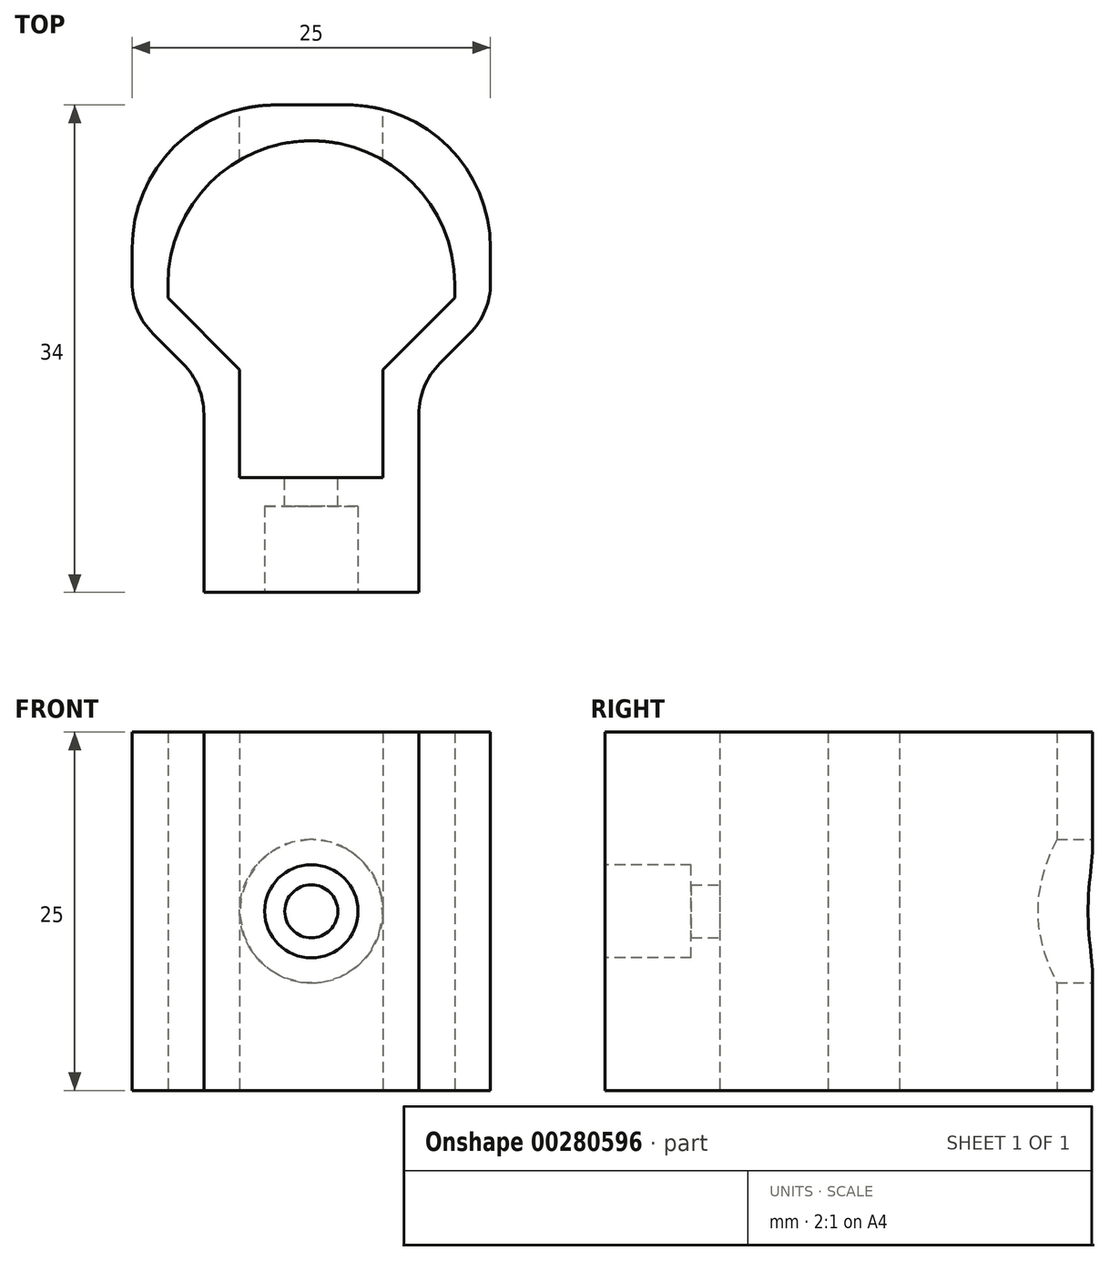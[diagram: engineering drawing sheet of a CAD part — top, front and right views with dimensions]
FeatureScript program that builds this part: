
annotation { "Feature Type Name" : "Feature", "Feature Type Description" : "" }
export const myFeature = defineFeature(function(context is Context, id is Id, definition is map)
    precondition{}
    {
        {
            var Q0;
            Q0=qCreatedBy(makeId("Top.planeOp"),FACE);
            var sketch = newSketch(context, id + "F0", { "sketchPlane" : qUnion([Q0])});
            skLineSegment(sketch, "E0", {"start": v(0, 0) * mm, "end": v(7.5, 0) * mm});
            skLineSegment(sketch, "E1", {"start": v(7.5, 0) * mm, "end": v(7.5, 14.5) * mm});
            skLineSegment(sketch, "E2", {"start": v(7.5, 14.5) * mm, "end": v(12.5, 14.5) * mm, "construction": true});
            skLineSegment(sketch, "E3", {"start": v(12.5, 14.5) * mm, "end": v(12.5, 19.5) * mm, "construction": true});
            skLineSegment(sketch, "E4", {"start": v(7.5, 14.5) * mm, "end": v(12.5, 19.5) * mm});
            skLineSegment(sketch, "E5", {"start": v(12.5, 34) * mm, "end": v(12.5, 19.5) * mm});
            skLineSegment(sketch, "E6", {"start": v(12.5, 34) * mm, "end": v(0, 34) * mm});
            skLineSegment(sketch, "E7.MirrorCS", {"start": v(-7.5, 14.5) * mm, "end": v(-12.5, 14.5) * mm, "construction": true});
            skLineSegment(sketch, "E8.MirrorCS", {"start": v(-12.5, 14.5) * mm, "end": v(-12.5, 19.5) * mm, "construction": true});
            skLineSegment(sketch, "E9.MirrorCS", {"start": v(-12.5, 34) * mm, "end": v(-12.5, 19.5) * mm});
            skLineSegment(sketch, "E10.MirrorCS", {"start": v(0, 0) * mm, "end": v(-7.5, 0) * mm});
            skLineSegment(sketch, "E11.MirrorCS", {"start": v(-7.5, 0) * mm, "end": v(-7.5, 14.5) * mm});
            skLineSegment(sketch, "E12.MirrorCS", {"start": v(-12.5, 34) * mm, "end": v(0, 34) * mm});
            skLineSegment(sketch, "E13.MirrorCS", {"start": v(-7.5, 14.5) * mm, "end": v(-12.5, 19.5) * mm});
            skLineSegment(sketch, "E14.0", {"start": v(-10, 21.5) * mm, "end": v(-10, 20.54) * mm});
            skLineSegment(sketch, "E14.1", {"start": v(-5, 15.54) * mm, "end": v(-10, 20.54) * mm});
            skLineSegment(sketch, "E14.2", {"start": v(0, 31.5) * mm, "end": v(0, 31.5) * mm});
            skLineSegment(sketch, "E14.3", {"start": v(-5, 8) * mm, "end": v(-5, 15.54) * mm});
            skLineSegment(sketch, "E14.6", {"start": v(0, 31.5) * mm, "end": v(0, 31.5) * mm});
            skLineSegment(sketch, "E14.7", {"start": v(10, 21.5) * mm, "end": v(10, 20.54) * mm});
            skLineSegment(sketch, "E14.8", {"start": v(5, 15.54) * mm, "end": v(10, 20.54) * mm});
            skLineSegment(sketch, "E14.9", {"start": v(5, 8) * mm, "end": v(5, 15.54) * mm});
            skLineSegment(sketch, "E15", {"start": v(-5, 8) * mm, "end": v(5, 8) * mm});
            skPoint(sketch, "E16.orphan", {"position": v(-5, 0.46) * mm});
            skPoint(sketch, "E17.orphan", {"position": v(5, 0.46) * mm});
            skPoint(sketch, "E18.visualSharp", {"position": v(-10, 31.5) * mm});
            skArc(sketch, "E18.filletArc", {"start": v(0, 31.5) * mm, "mid": v(-7.07, 28.57) * mm, "end": v(-10, 21.5) * mm});
            skPoint(sketch, "E19.visualSharp", {"position": v(10, 31.5) * mm});
            skArc(sketch, "E19.filletArc", {"start": v(10, 21.5) * mm, "mid": v(7.07, 28.57) * mm, "end": v(0, 31.5) * mm});
            skSolve(sketch);
        }
        {
            var Q0;
            Q0=makeQuery(id+"F0.imprint","IMPRINT",FACE,{"disambiguationData":[TD([[makeQuery(id+"F0.imprint","IMPRINT",EDGE,{"derivedFrom":sQuery(id+"F0.wireOp",EDGE,"E0")}),1.0]])]});
            extrude(context, id + "F1", {"entities" : qUnion([Q0]), "depth" : 25 * mm});
        }
        {
            var Q0;
            Q0=makeQuery(id+"F1.opExtrude","SWEPT_EDGE",EDGE,{"disambiguationData":[OSD([sQuery(id+"F0.wireOp",EDGE,"E9.MirrorCS"),sQuery(id+"F0.wireOp",EDGE,"E13.MirrorCS")])]});
            var Q1;
            Q1=makeQuery(id+"F1.opExtrude","SWEPT_EDGE",EDGE,{"disambiguationData":[OSD([sQuery(id+"F0.wireOp",EDGE,"E11.MirrorCS"),sQuery(id+"F0.wireOp",EDGE,"E13.MirrorCS")])]});
            var Q2;
            Q2=makeQuery(id+"F1.opExtrude","SWEPT_EDGE",EDGE,{"disambiguationData":[OSD([sQuery(id+"F0.wireOp",EDGE,"E4"),sQuery(id+"F0.wireOp",EDGE,"E5")])]});
            var Q3;
            Q3=makeQuery(id+"F1.opExtrude","SWEPT_EDGE",EDGE,{"disambiguationData":[OSD([sQuery(id+"F0.wireOp",EDGE,"E1"),sQuery(id+"F0.wireOp",EDGE,"E4")])]});
            fillet(context, id + "F2", {"entities" : qUnion([Q0, Q1, Q2, Q3]), "radius" : 5 * mm, "tangentPropagation" : true, "allowEdgeOverflow" : false});
        }
        {
            var Q0;
            Q0=makeQuery(id+"F1.opExtrude","SWEPT_FACE",FACE,{"disambiguationData":[OSD([sQuery(id+"F0.wireOp",EDGE,"E0"),sQuery(id+"F0.wireOp",EDGE,"E10.MirrorCS")])]});
            var sketch = newSketch(context, id + "F3", { "sketchPlane" : qUnion([Q0])});
            skLineSegment(sketch, "E20", {"start": v(-7.5, 25) * mm, "end": v(7.5, 0) * mm, "construction": true});
            skLineSegment(sketch, "E21", {"start": v(-7.5, 0) * mm, "end": v(7.5, 25) * mm, "construction": true});
            skCircle(sketch, "E22", {"center": v(0, 12.5) * mm, "radius": 3.25 * mm});
            skSolve(sketch);
        }
        {
            var Q0;
            Q0=makeQuery(id+"F3.imprint","IMPRINT",FACE,{"disambiguationData":[TD([[makeQuery(id+"F3.imprint","IMPRINT",EDGE,{"derivedFrom":sQuery(id+"F3.wireOp",EDGE,"E22")}),1.0]])]});
            extrude(context, id + "F4", {"entities" : qUnion([Q0]), "operationType" : NewBodyOperationType.REMOVE, "oppositeDirection" : true, "depth" : 6 * mm});
        }
        {
            var Q0;
            Q0=makeQuery(id+"F1.opExtrude","SWEPT_FACE",FACE,{"disambiguationData":[OSD([sQuery(id+"F0.wireOp",EDGE,"E15")])]});
            var sketch = newSketch(context, id + "F5", { "sketchPlane" : qUnion([Q0])});
            skLineSegment(sketch, "E23", {"start": v(-5, 25) * mm, "end": v(5, 0) * mm, "construction": true});
            skLineSegment(sketch, "E24", {"start": v(-5, 0) * mm, "end": v(5, 25) * mm, "construction": true});
            skCircle(sketch, "E25", {"center": v(0, 12.5) * mm, "radius": 1.85 * mm});
            skSolve(sketch);
        }
        {
            var Q0;
            Q0 = qSketchRegion(id + "F5", true);
            extrude(context, id + "F6", {"entities" : qUnion([Q0]), "operationType" : NewBodyOperationType.REMOVE, "oppositeDirection" : true, "depth" : 2 * mm});
        }
        {
            var Q0;
            Q0=makeQuery(id+"F1.opExtrude","SWEPT_FACE",FACE,{"disambiguationData":[OSD([sQuery(id+"F0.wireOp",EDGE,"E6"),sQuery(id+"F0.wireOp",EDGE,"E12.MirrorCS")])]});
            var sketch = newSketch(context, id + "F7", { "sketchPlane" : qUnion([Q0])});
            skLineSegment(sketch, "E26", {"start": v(-12.5, 25) * mm, "end": v(12.5, 0) * mm, "construction": true});
            skLineSegment(sketch, "E27", {"start": v(-12.5, 0) * mm, "end": v(12.5, 25) * mm, "construction": true});
            skCircle(sketch, "E28", {"center": v(0, 12.5) * mm, "radius": 5 * mm});
            skSolve(sketch);
        }
        {
            var Q0;
            Q0=makeQuery(id+"F7.imprint","IMPRINT",FACE,{"disambiguationData":[TD([[makeQuery(id+"F7.imprint","IMPRINT",EDGE,{"derivedFrom":sQuery(id+"F7.wireOp",EDGE,"E28")}),1.0]])]});
            extrude(context, id + "F8", {"entities" : qUnion([Q0]), "operationType" : NewBodyOperationType.REMOVE, "oppositeDirection" : true, "depth" : 8.9 * mm});
        }
        {
            var Q0;
            Q0=makeQuery(id+"F1.opExtrude","SWEPT_EDGE",EDGE,{"disambiguationData":[OSD([sQuery(id+"F0.wireOp",EDGE,"E9.MirrorCS"),sQuery(id+"F0.wireOp",EDGE,"E12.MirrorCS")])]});
            var Q1;
            Q1=makeQuery(id+"F1.opExtrude","SWEPT_EDGE",EDGE,{"disambiguationData":[OSD([sQuery(id+"F0.wireOp",EDGE,"E5"),sQuery(id+"F0.wireOp",EDGE,"E6")])]});
            fillet(context, id + "F9", {"entities" : qUnion([Q0, Q1]), "radius" : 10 * mm, "tangentPropagation" : true, "allowEdgeOverflow" : false});
        }
    });
